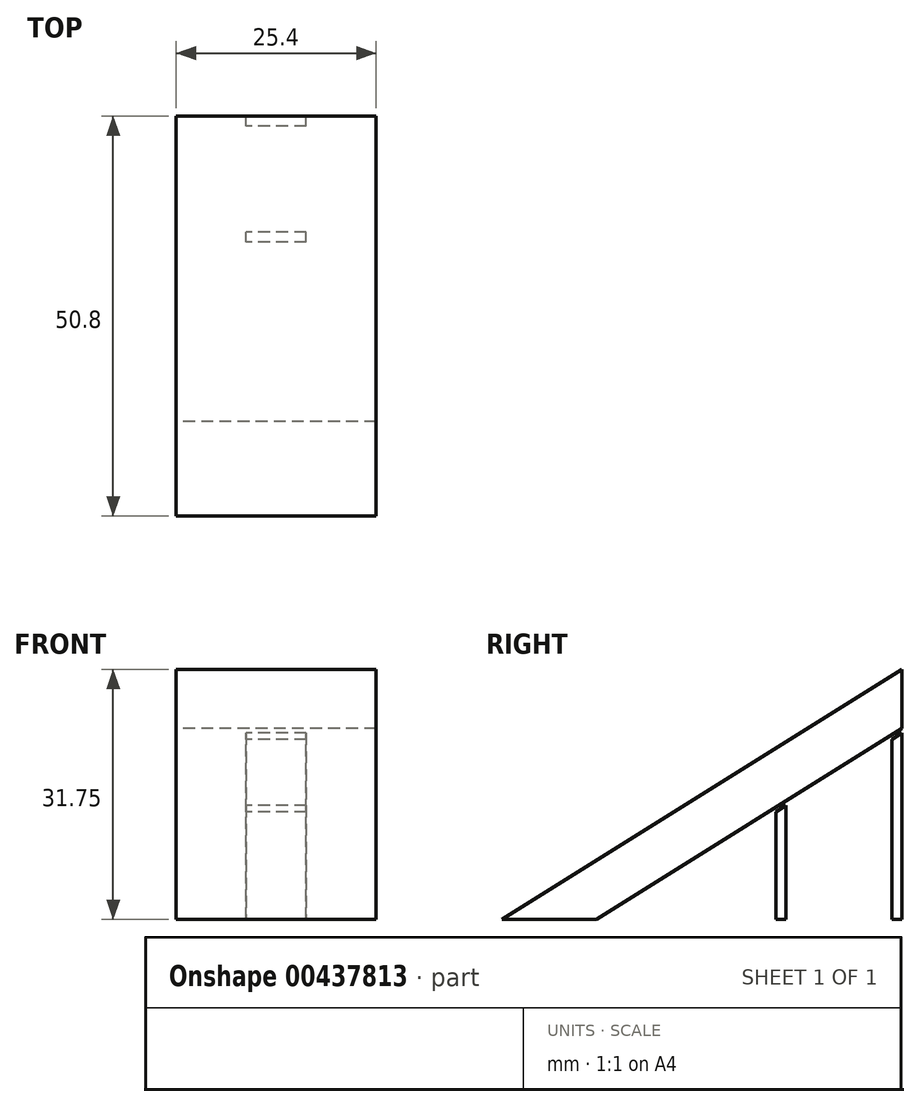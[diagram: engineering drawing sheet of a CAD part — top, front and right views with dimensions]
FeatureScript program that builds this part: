
annotation { "Feature Type Name" : "Feature", "Feature Type Description" : "" }
export const myFeature = defineFeature(function(context is Context, id is Id, definition is map)
    precondition{}
    {
        {
            var Q0;
            Q0=qCreatedBy(makeId("Right.planeOp"),FACE);
            var sketch = newSketch(context, id + "F0", { "sketchPlane" : qUnion([Q0])});
            skLineSegment(sketch, "E0", {"start": v(0, 24.26) * mm, "end": v(0, 31.75) * mm});
            skLineSegment(sketch, "E1", {"start": v(-50.8, 0) * mm, "end": v(-38.82, 0) * mm});
            skLineSegment(sketch, "E2", {"start": v(0, 31.75) * mm, "end": v(-50.8, 0) * mm});
            skLineSegment(sketch, "E3.0", {"start": v(0, 24.26) * mm, "end": v(-38.82, 0) * mm});
            skSolve(sketch);
        }
        {
            var Q0;
            Q0=qCreatedBy(makeId("Right.planeOp"),FACE);
            var sketch = newSketch(context, id + "F1", { "sketchPlane" : qUnion([Q0])});
            skLineSegment(sketch, "E4.0", {"start": v(0.27, 23.83) * mm, "end": v(-38.55, -0.43) * mm, "construction": true});
            skLineSegment(sketch, "E5", {"start": v(0, 23.66) * mm, "end": v(0, 0) * mm});
            skLineSegment(sketch, "E6", {"start": v(0, 0) * mm, "end": v(-1.27, 0) * mm});
            skLineSegment(sketch, "E7", {"start": v(-1.27, 0) * mm, "end": v(-1.27, 22.87) * mm});
            skLineSegment(sketch, "E8", {"start": v(-1.27, 22.87) * mm, "end": v(0, 23.66) * mm});
            skLineSegment(sketch, "E9", {"start": v(-14.73, 14.45) * mm, "end": v(-14.73, 0) * mm});
            skLineSegment(sketch, "E10", {"start": v(-14.73, 0) * mm, "end": v(-16, 0) * mm});
            skLineSegment(sketch, "E11", {"start": v(-16, 0) * mm, "end": v(-16, 13.66) * mm});
            skLineSegment(sketch, "E12", {"start": v(-16, 13.66) * mm, "end": v(-14.73, 14.45) * mm});
            skSolve(sketch);
        }
        {
            var Q0;
            Q0 = qSketchRegion(id + "F0", true);
            extrude(context, id + "F2", {"entities" : qUnion([Q0]), "endBound" : BoundingType.SYMMETRIC, "depth" : 25.4 * mm});
        }
        {
            var Q0;
            Q0 = qSketchRegion(id + "F1", true);
            extrude(context, id + "F3", {"entities" : qUnion([Q0]), "endBound" : BoundingType.SYMMETRIC, "depth" : 7.62 * mm});
        }
    });
